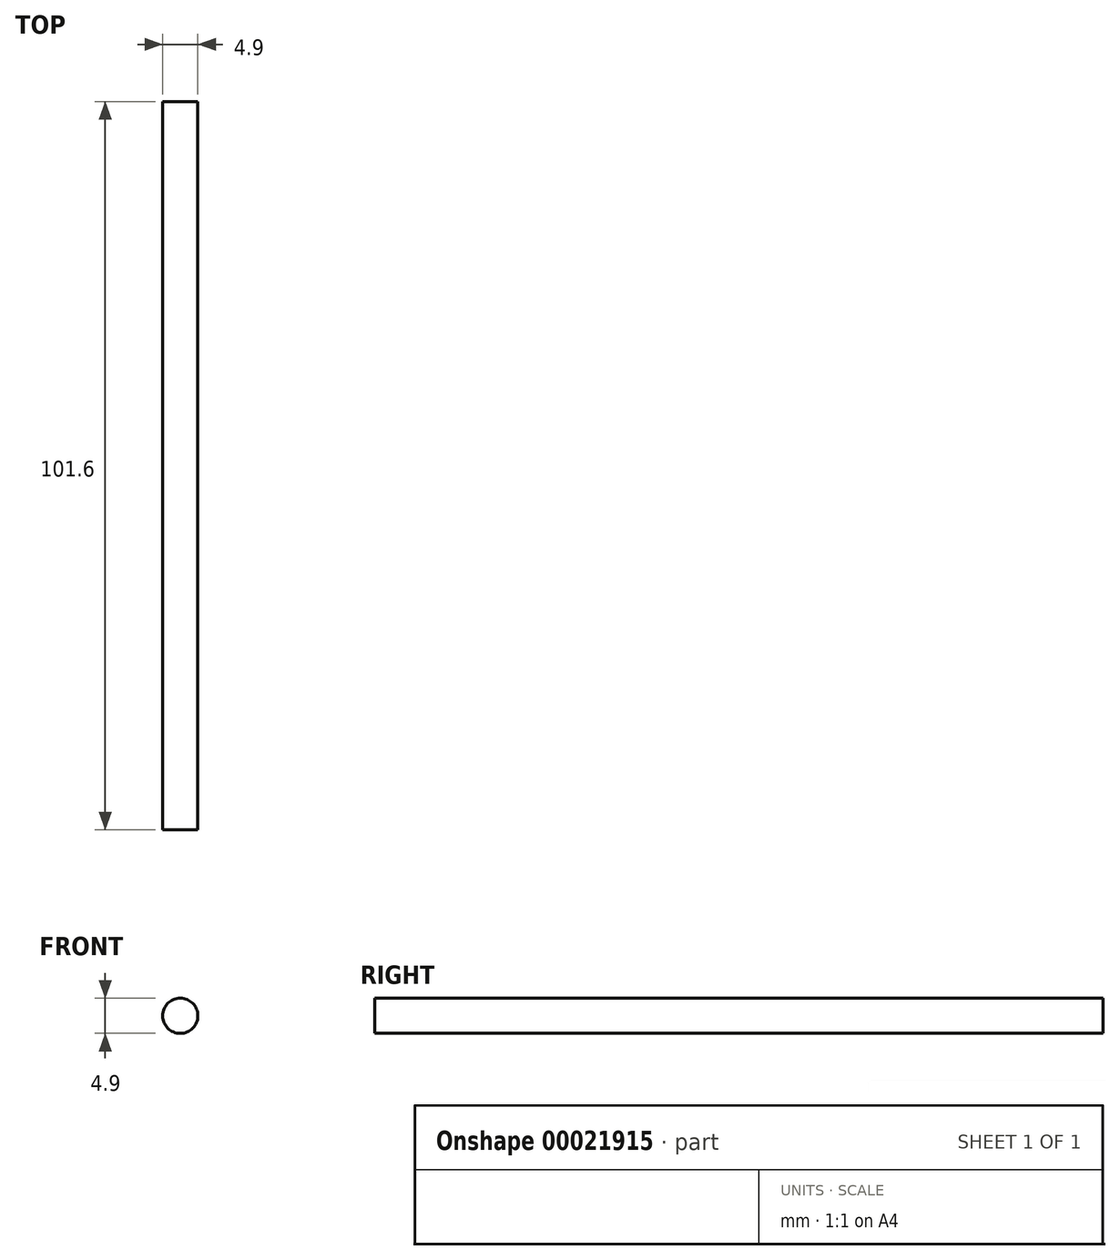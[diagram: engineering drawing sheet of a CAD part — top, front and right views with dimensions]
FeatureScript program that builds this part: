
annotation { "Feature Type Name" : "Feature", "Feature Type Description" : "" }
export const myFeature = defineFeature(function(context is Context, id is Id, definition is map)
    precondition{}
    {
        {
            var Q0;
            Q0=qCreatedBy(makeId("Front.planeOp"),FACE);
            var sketch = newSketch(context, id + "F0", { "sketchPlane" : qUnion([Q0])});
            skCircle(sketch, "E0", {"center": v(0, 0) * mm, "radius": 2.45 * mm});
            skSolve(sketch);
        }
        {
            var Q0;
            Q0=qSketchRegion(id+"F0",true);
            extrude(context, id + "F1", {"entities" : qUnion([Q0]), "depth" : 101.6 * mm});
        }
    });
